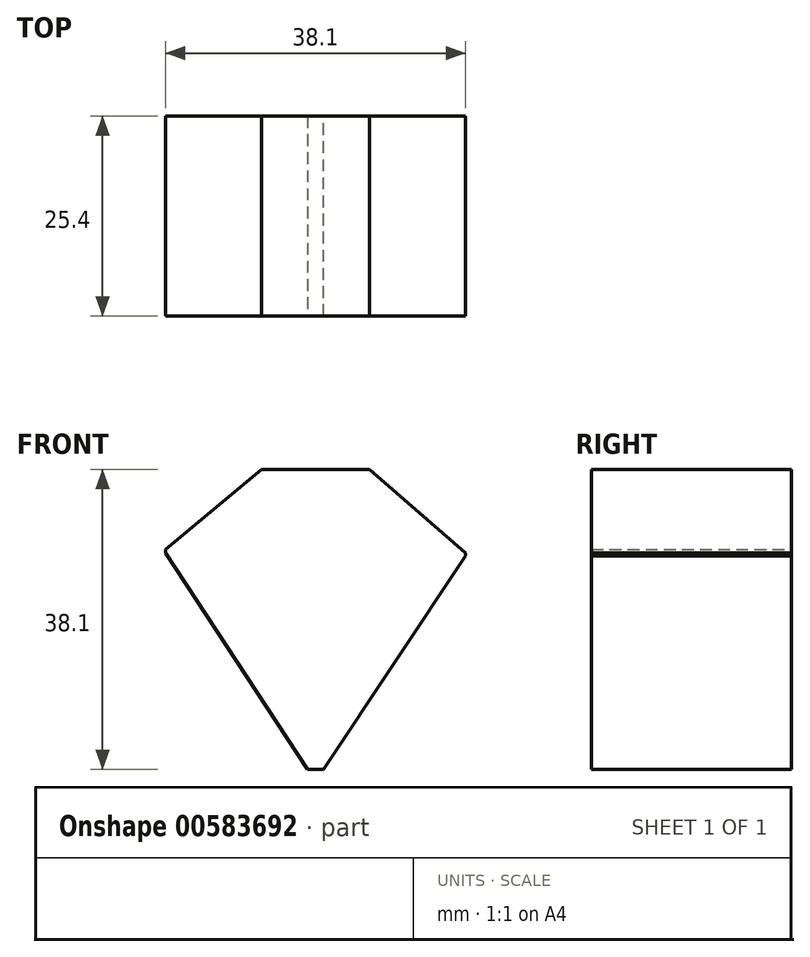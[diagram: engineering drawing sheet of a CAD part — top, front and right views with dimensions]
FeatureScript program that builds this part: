
annotation { "Feature Type Name" : "Feature", "Feature Type Description" : "" }
export const myFeature = defineFeature(function(context is Context, id is Id, definition is map)
    precondition{}
    {
        {
            var Q0;
            Q0=qCreatedBy(makeId("Front.planeOp"),FACE);
            var sketch = newSketch(context, id + "F0", { "sketchPlane" : qUnion([Q0])});
            skLineSegment(sketch, "E0.bottom", {"start": v(19.05, 19.05) * mm, "end": v(-19.05, 19.05) * mm});
            skLineSegment(sketch, "E0.top", {"start": v(19.05, -19.05) * mm, "end": v(-19.05, -19.05) * mm});
            skLineSegment(sketch, "E0.left", {"start": v(19.05, 19.05) * mm, "end": v(19.05, -19.05) * mm});
            skLineSegment(sketch, "E0.right", {"start": v(-19.05, 19.05) * mm, "end": v(-19.05, -19.05) * mm});
            skPoint(sketch, "E0.middle", {"position": v(0, 0) * mm});
            skSolve(sketch);
        }
        {
            var Q0;
            Q0 = qSketchRegion(id + "F0", true);
            extrude(context, id + "F1", {"entities" : qUnion([Q0]), "depth" : 25.4 * mm, "offsetDistance" : 25.4 * mm});
        }
        {
            var Q0;
            Q0=qCreatedBy(makeId("Front.planeOp"),FACE);
            var sketch = newSketch(context, id + "F2", { "sketchPlane" : qUnion([Q0])});
            skLineSegment(sketch, "E1", {"start": v(-6.47, 19.4) * mm, "end": v(-22.7, 5.87) * mm});
            skLineSegment(sketch, "E2", {"start": v(6.47, 19.4) * mm, "end": v(28.73, 0) * mm});
            skLineSegment(sketch, "E3", {"start": v(-19.25, 8.75) * mm, "end": v(0, -20.6) * mm});
            skLineSegment(sketch, "E4", {"start": v(0, -20.6) * mm, "end": v(19.2, 8.3) * mm});
            skLineSegment(sketch, "E5", {"start": v(-19.25, 8.75) * mm, "end": v(-27.52, 26.92) * mm});
            skLineSegment(sketch, "E6", {"start": v(-27.52, 26.92) * mm, "end": v(-6.47, 19.4) * mm});
            skLineSegment(sketch, "E7", {"start": v(6.47, 19.4) * mm, "end": v(24.51, 32.94) * mm});
            skLineSegment(sketch, "E8", {"start": v(24.51, 32.94) * mm, "end": v(28.73, 0) * mm});
            skLineSegment(sketch, "E9", {"start": v(0, -20.6) * mm, "end": v(26.37, -38.12) * mm});
            skLineSegment(sketch, "E10", {"start": v(26.37, -38.12) * mm, "end": v(19.2, 8.3) * mm});
            skLineSegment(sketch, "E11", {"start": v(-19.25, 8.75) * mm, "end": v(-33.24, -26.62) * mm});
            skLineSegment(sketch, "E12", {"start": v(-33.24, -26.62) * mm, "end": v(0, -20.6) * mm});
            skSolve(sketch);
        }
        {
            var Q0;
            Q0 = qSketchRegion(id + "F2", true);
            extrude(context, id + "F3", {"entities" : qUnion([Q0]), "operationType" : NewBodyOperationType.REMOVE, "endBound" : BoundingType.THROUGH_ALL, "depth" : 25.4 * mm, "offsetDistance" : 25.4 * mm});
        }
    });
